# Revit family: Fireplace_Gas_Heatilator_Rave
name_source: partatom
category: Mechanical Equipment
revit_build: Autodesk Revit 2015 (Build: 20140323_1530(x64)
units: mm (PartAtom-declared; Revit-internal decimal feet)

## types (4) — shared parameters
Assembly Code = D3020
Construction Details = http://www.arcat.com
Default Elevation = 0' - 0"
Electrical_Voltage = 120 V
Fixture Finish = Metal - Heatilator - Metallic Black
Fuel Consumption = as Specified
HVAC_BTU Output = 0.0 Btu/h
Heating Capacity = as Specified
Keynote = 10305
Manufacturer = Heatilator
Manufacturer Website = http://www.heatilator.com
Opening Height = 1' - 1 1/4"
Product Data = http://www.arcat.com
Revision = R2_2014-09
Sales Information = http://www.heatilator.com
Send Message = http://www.arcat.com
Specification = http://www.arcat.com
Standards Conformance = UL  ;  cUL
URL = http://www.heatilator.com
Unit Depth = 1' - 6 1/4"
zero-valued in all types: Expected Lifespan (Years), Maintenance Schedule (Months), Unit Weight, Warranty Duration (Years)

## per-type parameters (varying)
| type | Description | Efficiency Ratings | Fuel Type | HVAC_BTU Input | Model | Opening Width | Rear Width | Unit Height | Unit Width |
| 43x13 Viewing Area LP | Heatilator Gas Burning Fireplace - Rave RAVE4013i LP as Specified | Steady State 75.3  ;  AFUE 59.5  ;  EnerGuide 60.6 | LP | 25000.0 Btu/h | RAVE4013i | 3' - 7" | 3' - 1 3/4" | 3' - 5 3/4" | 4' - 0" |
| 43x13 Viewing Area NG | Heatilator Gas Burning Fireplace - Rave RAVE4013i NG as Specified | Steady State 75.3  ;  AFUE 59.5  ;  EnerGuide 60.6 | NG | 26000.0 Btu/h | RAVE4013i | 3' - 7" | 3' - 1 3/4" | 3' - 5 3/4" | 4' - 0" |
| 31x13 Viewing Area LP | Heatilator Gas Burning Fireplace - Rave RAVE3012i LP as Specified | Steady State 60.5  ;  AFUE 57.4  ;  EnerGuide 57.4 | LP | 17500.0 Btu/h | RAVE3012i | 2' - 7" | 2' - 1 3/4" | 3' - 1" | 3' - 3" |
| 31x13 Viewing Area NG | Heatilator Gas Burning Fireplace - Rave RAVE3012i NG as Specified | Steady State 60.5  ;  AFUE 57.4  ;  EnerGuide 57.4 | NG | 20000.0 Btu/h | RAVE3012i | 2' - 7" | 2' - 1 3/4" | 3' - 1" | 3' - 3" |

## geometry (parser evidence)
native form markers: Blend x4, Sweep x6
no freeform markers — native parametric forms only
